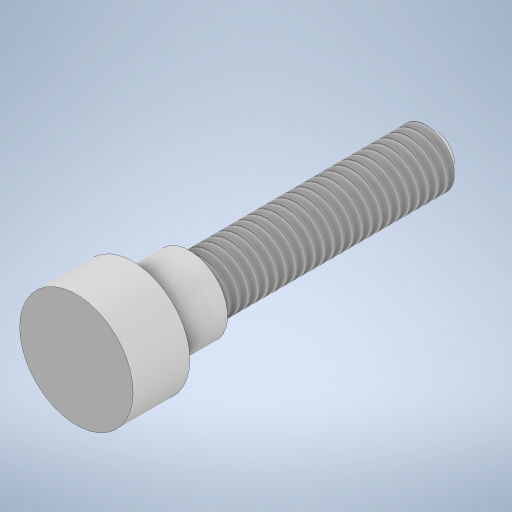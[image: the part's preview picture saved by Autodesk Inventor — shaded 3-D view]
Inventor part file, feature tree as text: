
AUTODESK INVENTOR PART (.ipt)
format: ipt  version: 2023 (Build 270158000, 158)  size: 273,408 bytes
history: native  units: mm
features: other x1, revolve x1, thread x1, chamfer x1, sketch x1
ambient origin geometry x8: Origin, YZ Plane, XZ Plane, XY Plane, X Axis, Y Axis, Z Axis, Center Point
bodies: Body1 (feature_tree)
feature tree (5):
  other  "Твердое тело1"
  revolve  "Вращение1"
  thread  "Резьба1"
  chamfer  "Фаска1"  Distance=3.0mm
  sketch  "Эскиз1"
